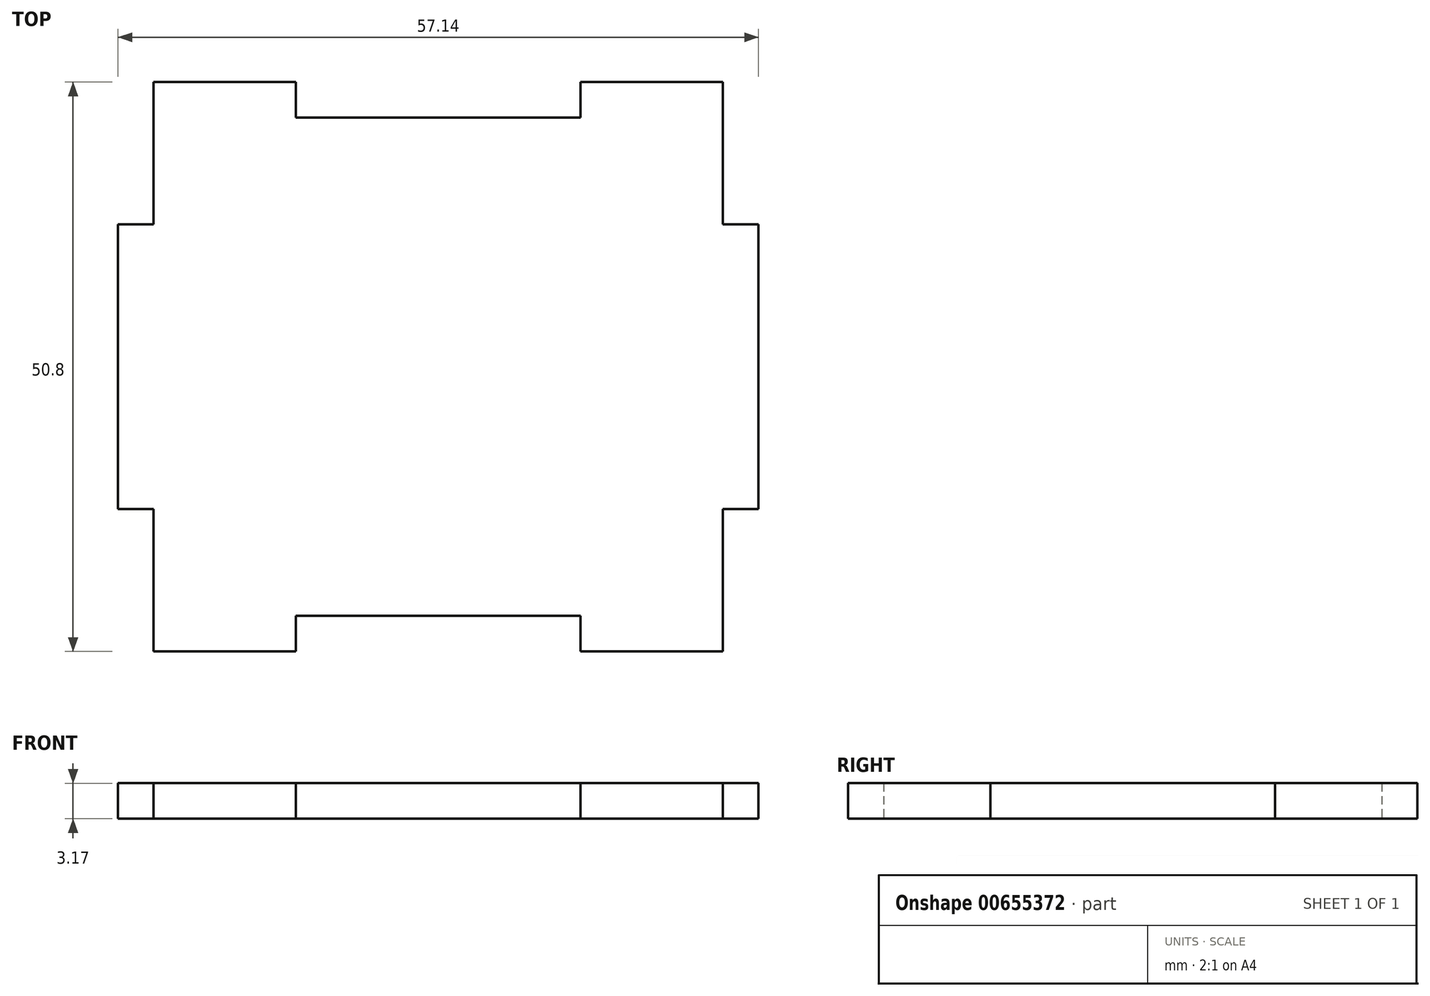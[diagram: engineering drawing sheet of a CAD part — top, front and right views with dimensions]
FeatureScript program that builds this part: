
annotation { "Feature Type Name" : "Feature", "Feature Type Description" : "" }
export const myFeature = defineFeature(function(context is Context, id is Id, definition is map)
    precondition{}
    {
        {
            var Q0;
            Q0=qCreatedBy(makeId("Top.planeOp"),FACE);
            var sketch = newSketch(context, id + "F0", { "sketchPlane" : qUnion([Q0])});
            skLineSegment(sketch, "E0.bottom", {"start": v(25.4, 25.4) * mm, "end": v(-25.4, 25.4) * mm});
            skLineSegment(sketch, "E0.top", {"start": v(25.4, -25.4) * mm, "end": v(-25.4, -25.4) * mm});
            skLineSegment(sketch, "E0.left", {"start": v(25.4, 25.4) * mm, "end": v(25.4, -25.4) * mm});
            skLineSegment(sketch, "E0.right", {"start": v(-25.4, 25.4) * mm, "end": v(-25.4, -25.4) * mm});
            skPoint(sketch, "E0.middle", {"position": v(0, 0) * mm});
            skLineSegment(sketch, "E1.bottom", {"start": v(12.7, 22.22) * mm, "end": v(-12.7, 22.22) * mm});
            skLineSegment(sketch, "E1.top", {"start": v(12.7, 28.58) * mm, "end": v(-12.7, 28.58) * mm});
            skLineSegment(sketch, "E1.left", {"start": v(12.7, 22.23) * mm, "end": v(12.7, 28.58) * mm});
            skLineSegment(sketch, "E1.right", {"start": v(-12.7, 22.22) * mm, "end": v(-12.7, 28.57) * mm});
            skPoint(sketch, "E1.middle", {"position": v(0, 25.4) * mm});
            skLineSegment(sketch, "E2.bottom", {"start": v(28.57, 12.7) * mm, "end": v(22.22, 12.7) * mm});
            skLineSegment(sketch, "E2.top", {"start": v(28.57, -12.7) * mm, "end": v(22.22, -12.7) * mm});
            skLineSegment(sketch, "E2.left", {"start": v(28.57, 12.7) * mm, "end": v(28.57, -12.7) * mm});
            skLineSegment(sketch, "E2.right", {"start": v(22.22, 12.7) * mm, "end": v(22.22, -12.7) * mm});
            skPoint(sketch, "E2.middle", {"position": v(25.4, 0) * mm});
            skLineSegment(sketch, "E3.bottom", {"start": v(-22.22, 12.7) * mm, "end": v(-28.57, 12.7) * mm});
            skLineSegment(sketch, "E3.top", {"start": v(-22.22, -12.7) * mm, "end": v(-28.57, -12.7) * mm});
            skLineSegment(sketch, "E3.left", {"start": v(-22.22, 12.7) * mm, "end": v(-22.22, -12.7) * mm});
            skLineSegment(sketch, "E3.right", {"start": v(-28.57, 12.7) * mm, "end": v(-28.57, -12.7) * mm});
            skPoint(sketch, "E3.middle", {"position": v(-25.4, 0) * mm});
            skLineSegment(sketch, "E4.bottom", {"start": v(12.7, -22.23) * mm, "end": v(-12.7, -22.23) * mm});
            skLineSegment(sketch, "E4.top", {"start": v(12.7, -28.58) * mm, "end": v(-12.7, -28.58) * mm});
            skLineSegment(sketch, "E4.left", {"start": v(12.7, -22.23) * mm, "end": v(12.7, -28.58) * mm});
            skLineSegment(sketch, "E4.right", {"start": v(-12.7, -22.23) * mm, "end": v(-12.7, -28.58) * mm});
            skPoint(sketch, "E4.middle", {"position": v(0, -25.4) * mm});
            skSolve(sketch);
        }
        {
            var Q0;
            {var subQ0=sQuery(id+"F0.wireOp",EDGE,"E1.bottom");Q0=makeQuery(id+"F0.imprint","IMPRINT",FACE,{"disambiguationData":[TD([[makeQuery(id+"F0.imprint","IMPRINT",EDGE,{"derivedFrom":subQ0}),1.0]])]});}
            var Q1;
            {var subQ5=sQuery(id+"F0.wireOp",EDGE,"E3.right");Q1=makeQuery(id+"F0.imprint","IMPRINT",FACE,{"disambiguationData":[TD([[makeQuery(id+"F0.imprint","IMPRINT",EDGE,{"derivedFrom":subQ5}),1.0]])]});}
            var Q2;
            {var subQ5=sQuery(id+"F0.wireOp",EDGE,"E3.left");Q2=makeQuery(id+"F0.imprint","IMPRINT",FACE,{"disambiguationData":[TD([[makeQuery(id+"F0.imprint","IMPRINT",EDGE,{"derivedFrom":subQ5}),-1.0]])]});}
            var Q3;
            {var subQ5=sQuery(id+"F0.wireOp",EDGE,"E2.left");Q3=makeQuery(id+"F0.imprint","IMPRINT",FACE,{"disambiguationData":[TD([[makeQuery(id+"F0.imprint","IMPRINT",EDGE,{"derivedFrom":subQ5}),-1.0]])]});}
            var Q4;
            {var subQ5=sQuery(id+"F0.wireOp",EDGE,"E2.right");Q4=makeQuery(id+"F0.imprint","IMPRINT",FACE,{"disambiguationData":[TD([[makeQuery(id+"F0.imprint","IMPRINT",EDGE,{"derivedFrom":subQ5}),1.0]])]});}
            extrude(context, id + "F1", {"entities" : qUnion([Q0, Q1, Q2, Q3, Q4]), "depth" : 3.17 * mm, "offsetDistance" : 25.4 * mm});
        }
    });
